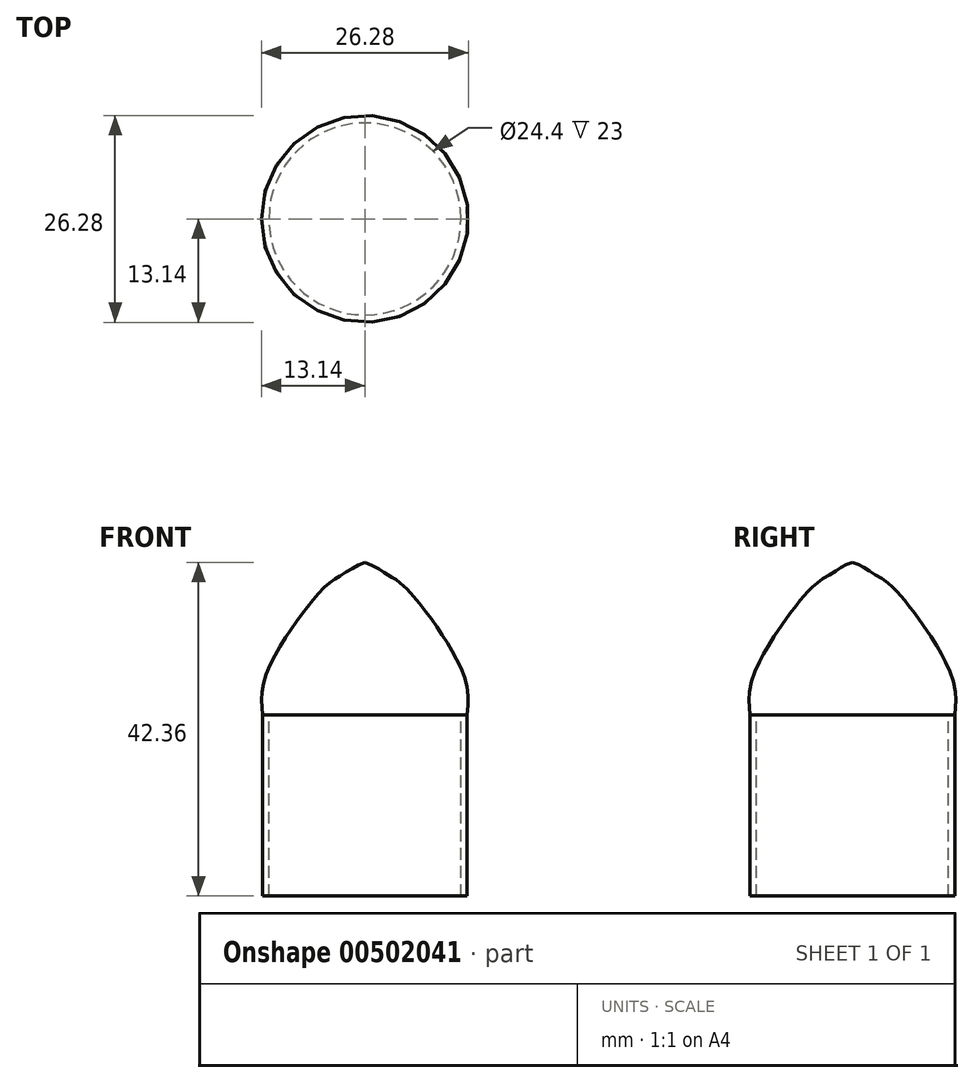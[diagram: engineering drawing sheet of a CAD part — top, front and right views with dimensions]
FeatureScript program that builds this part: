
annotation { "Feature Type Name" : "Feature", "Feature Type Description" : "" }
export const myFeature = defineFeature(function(context is Context, id is Id, definition is map)
    precondition{}
    {
        {
            var Q0;
            Q0=qCreatedBy(makeId("Front.planeOp"),FACE);
            var sketch = newSketch(context, id + "F0", { "sketchPlane" : qUnion([Q0])});
            skLineSegment(sketch, "E0", {"start": v(-12.2, 0) * mm, "end": v(-12.2, 23) * mm});
            skLineSegment(sketch, "E1", {"start": v(-13, 0) * mm, "end": v(-13, 23) * mm});
            skLineSegment(sketch, "E2", {"start": v(-12.2, 0) * mm, "end": v(-13, 0) * mm});
            skFitSpline(sketch, "E3", {"points": [v(-13, 23) * mm, v(-13, 26.53) * mm, v(-10.53, 32.07) * mm, v(-7.44, 36.53) * mm, v(-4.7, 39.61) * mm, v(-2.64, 40.98) * mm, v(0, 42.36) * mm], "startDerivative": vector(-1.61, 21.58) * mm, "endDerivative": vector(16.92, 3.82) * mm});
            skLineSegment(sketch, "E4", {"start": v(-12.2, 23) * mm, "end": v(0, 23) * mm});
            skLineSegment(sketch, "E5", {"start": v(0, 47.54) * mm, "end": v(0, -7.92) * mm});
            skLineSegment(sketch, "E6", {"start": v(0, 47.54) * mm, "end": v(0, 12.51) * mm});
            skSolve(sketch);
        }
        {
            var Q0;
            Q0=makeQuery(id+"F0.imprint","IMPRINT",FACE,{"disambiguationData":[TD([[makeQuery(id+"F0.imprint","IMPRINT",EDGE,{"derivedFrom":sQuery(id+"F0.wireOp",EDGE,"E0")}),1.0]])]});
            var Q1;
            Q1=sQuery(id+"F0.wireOp",EDGE,"E6");
            revolve(context, id + "F1", {"entities" : qUnion([Q0]), "axis" : qUnion([Q1]), "revolveType" : RevolveType.FULL});
        }
    });
